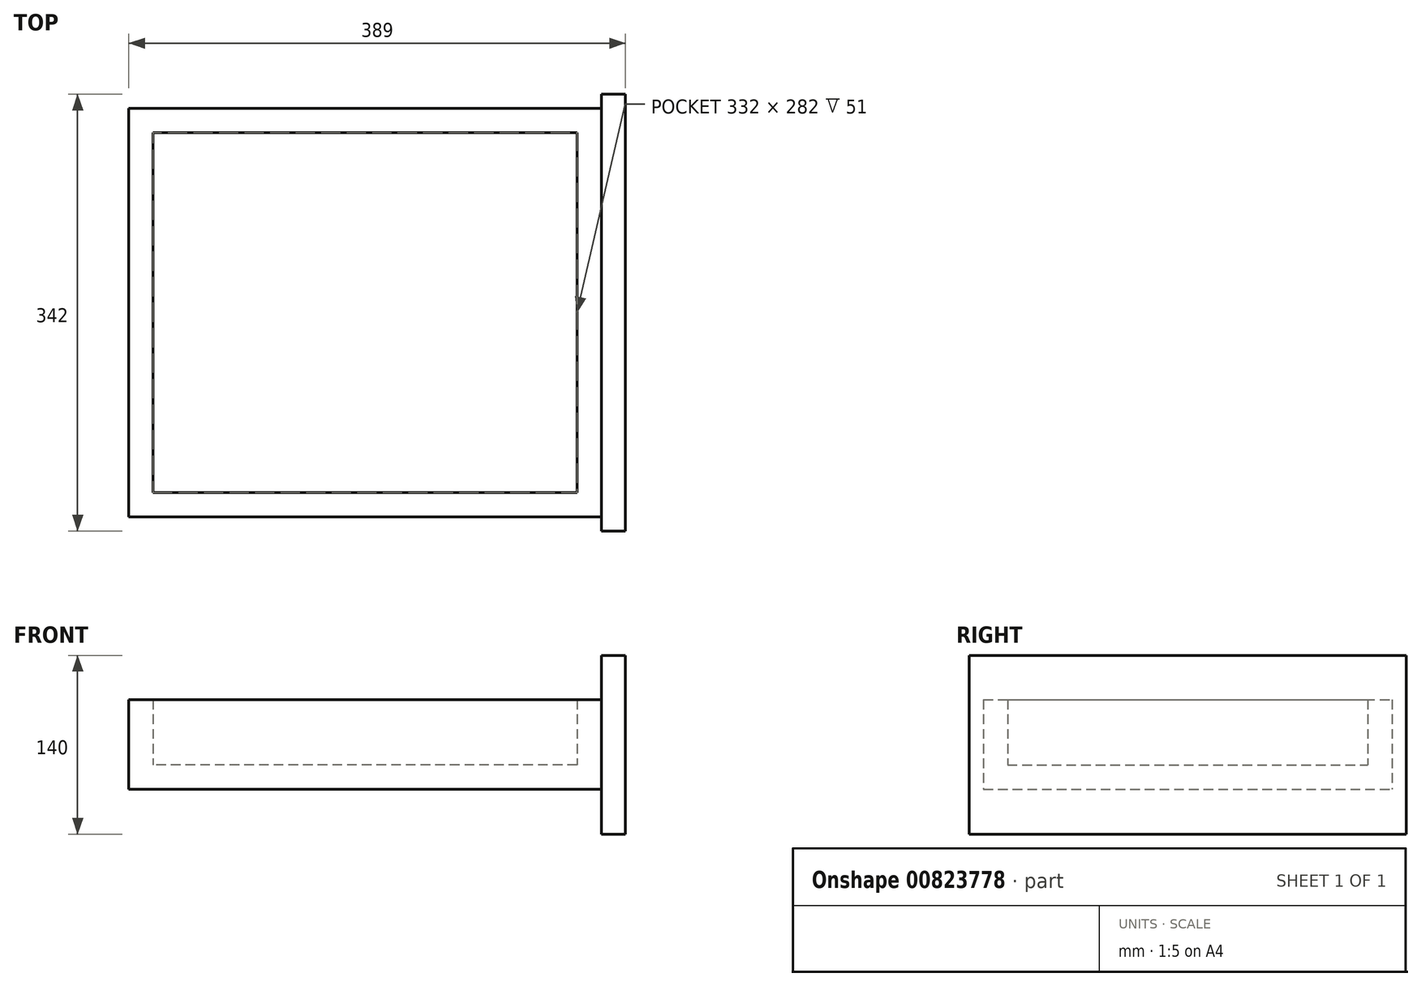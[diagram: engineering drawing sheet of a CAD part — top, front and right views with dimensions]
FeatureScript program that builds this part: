
annotation { "Feature Type Name" : "Feature", "Feature Type Description" : "" }
export const myFeature = defineFeature(function(context is Context, id is Id, definition is map)
    precondition{}
    {
        {
            var Q0;
            Q0=qCreatedBy(makeId("Top.planeOp"),FACE);
            var sketch = newSketch(context, id + "F0", { "sketchPlane" : qUnion([Q0])});
            skLineSegment(sketch, "E0.bottom", {"start": v(185, -160) * mm, "end": v(-185, -160) * mm});
            skLineSegment(sketch, "E0.top", {"start": v(185, 160) * mm, "end": v(-185, 160) * mm});
            skLineSegment(sketch, "E0.left", {"start": v(185, -160) * mm, "end": v(185, 160) * mm});
            skLineSegment(sketch, "E0.right", {"start": v(-185, -160) * mm, "end": v(-185, 160) * mm});
            skPoint(sketch, "E0.middle", {"position": v(0, 0) * mm});
            skSolve(sketch);
        }
        {
            var Q0;
            Q0=makeQuery(id+"F0.imprint","IMPRINT",FACE,{"disambiguationData":[TD([[makeQuery(id+"F0.imprint","IMPRINT",EDGE,{"derivedFrom":sQuery(id+"F0.wireOp",EDGE,"E0.bottom")}),-1.0]])]});
            var sketch = newSketch(context, id + "F1", { "sketchPlane" : qUnion([Q0])});
            skLineSegment(sketch, "E1.bottom", {"start": v(166, -141) * mm, "end": v(-166, -141) * mm});
            skLineSegment(sketch, "E1.top", {"start": v(166, 141) * mm, "end": v(-166, 141) * mm});
            skLineSegment(sketch, "E1.left", {"start": v(166, -141) * mm, "end": v(166, 141) * mm});
            skLineSegment(sketch, "E1.right", {"start": v(-166, -141) * mm, "end": v(-166, 141) * mm});
            skPoint(sketch, "E1.middle", {"position": v(0, 0) * mm});
            skSolve(sketch);
        }
        {
            var Q0;
            Q0=makeQuery(id+"F1.imprint","IMPRINT",FACE,{"disambiguationData":[TD([[makeQuery(id+"F1.imprint","IMPRINT",EDGE,{"derivedFrom":sQuery(id+"F1.wireOp",EDGE,"E1.bottom")}),1.0]])]});
            extrude(context, id + "F2", {"entities" : qUnion([Q0]), "depth" : 70 * mm, "offsetDistance" : 25 * mm});
        }
        {
            var Q0;
            Q0=makeQuery(id+"F0.imprint","IMPRINT",FACE,{"disambiguationData":[TD([[makeQuery(id+"F0.imprint","IMPRINT",EDGE,{"derivedFrom":sQuery(id+"F0.wireOp",EDGE,"E0.bottom")}),-1.0]])]});
            extrude(context, id + "F3", {"entities" : qUnion([Q0]), "operationType" : NewBodyOperationType.ADD, "depth" : 19 * mm, "offsetDistance" : 25 * mm});
        }
        {
            var Q0;
            Q0=makeQuery(id+"F2.opExtrude","SWEPT_FACE",FACE,{"disambiguationData":[OSD([sQuery(id+"F0.wireOp",EDGE,"E0.left")])]});
            var sketch = newSketch(context, id + "F4", { "sketchPlane" : qUnion([Q0])});
            skLineSegment(sketch, "E2.bottom", {"start": v(-171, -35.2) * mm, "end": v(171, -35.2) * mm});
            skLineSegment(sketch, "E2.top", {"start": v(-171, 104.8) * mm, "end": v(171, 104.8) * mm});
            skLineSegment(sketch, "E2.left", {"start": v(-171, -35.2) * mm, "end": v(-171, 104.8) * mm});
            skLineSegment(sketch, "E2.right", {"start": v(171, -35.2) * mm, "end": v(171, 104.8) * mm});
            skPoint(sketch, "E2.middle", {"position": v(0, 34.8) * mm});
            skSolve(sketch);
        }
        {
            var Q0;
            Q0=makeQuery(id+"F4.imprint","IMPRINT",FACE,{"disambiguationData":[TD([[makeQuery(id+"F4.imprint","IMPRINT",EDGE,{"derivedFrom":sQuery(id+"F4.wireOp",EDGE,"E2.bottom")}),1.0]])]});
            var Q1;
            {var subQ0=sQuery(id+"F0.wireOp",EDGE,"E0.left");Q1=makeQuery(id+"F4.imprint","IMPRINT",FACE,{"disambiguationData":[TD([[makeQuery(id+"F4.imprint","IMPRINT",EDGE,{"derivedFrom":makeQuery(id+"F2.opExtrude","CAP_EDGE",EDGE,{"disambiguationData":[OSD([subQ0])],"isStart":true})}),1.0]])]});}
            extrude(context, id + "F5", {"entities" : qUnion([Q0, Q1]), "operationType" : NewBodyOperationType.ADD, "depth" : 19 * mm, "offsetDistance" : 25 * mm});
        }
    });
